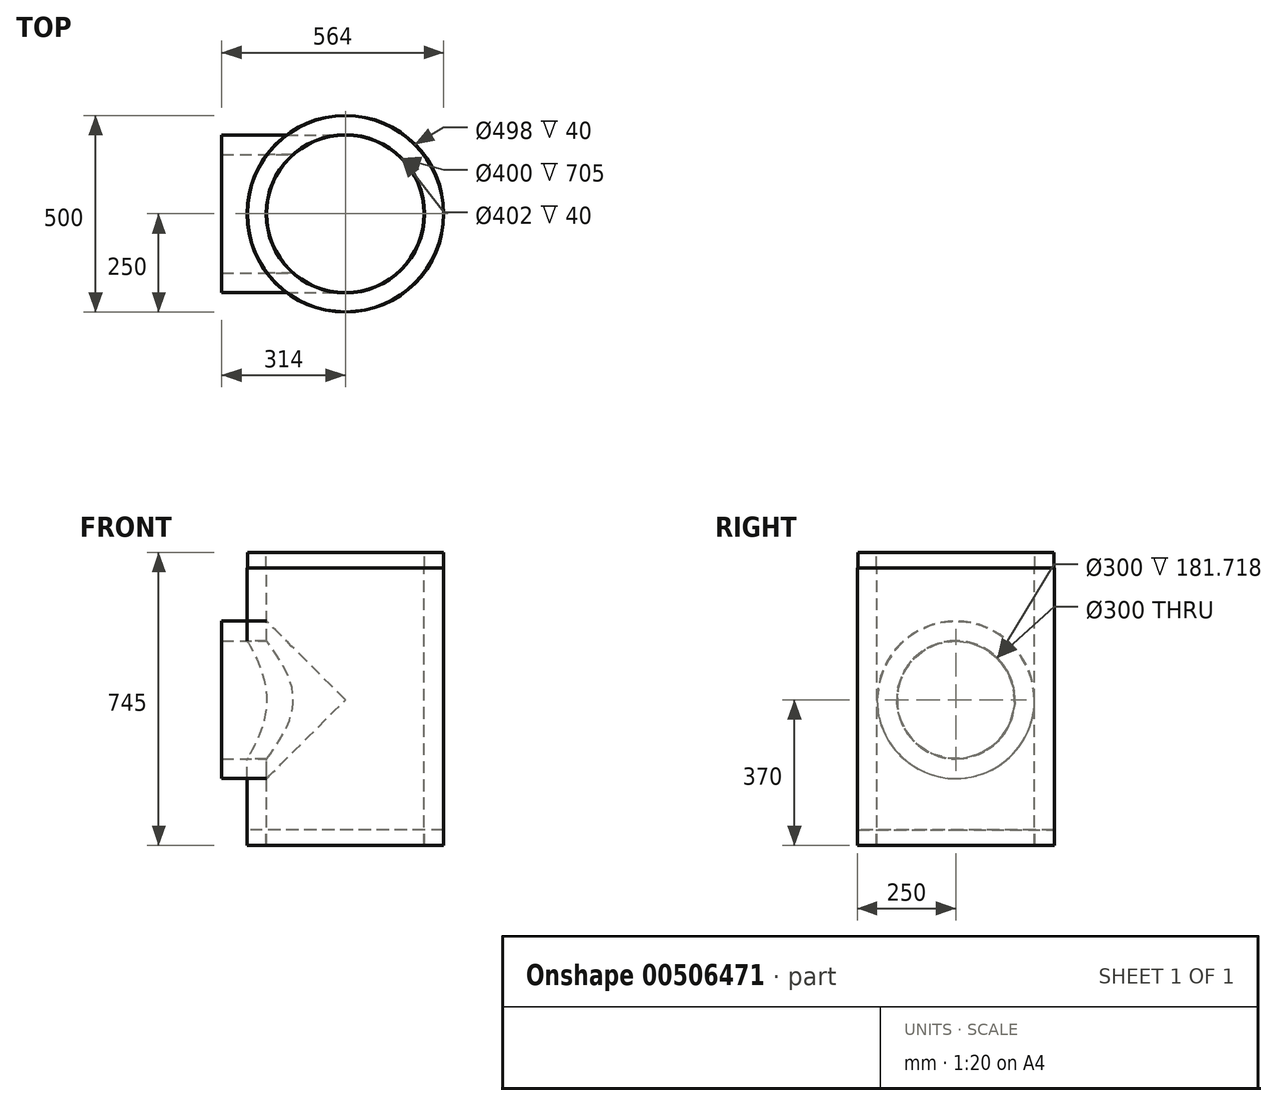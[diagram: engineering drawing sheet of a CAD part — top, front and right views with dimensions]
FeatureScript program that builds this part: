
annotation { "Feature Type Name" : "Feature", "Feature Type Description" : "" }
export const myFeature = defineFeature(function(context is Context, id is Id, definition is map)
    precondition{}
    {
        {
            var Q0;
            Q0=qCreatedBy(makeId("Front.planeOp"),FACE);
            var sketch = newSketch(context, id + "F0", { "sketchPlane" : qUnion([Q0])});
            skLineSegment(sketch, "E0", {"start": v(0, 722.18) * mm, "end": v(0, -793.11) * mm, "construction": true});
            skLineSegment(sketch, "E1", {"start": v(-200, -370) * mm, "end": v(-200, 335) * mm});
            skLineSegment(sketch, "E2", {"start": v(-200, 335) * mm, "end": v(-201, 335) * mm});
            skLineSegment(sketch, "E3", {"start": v(-201, 335) * mm, "end": v(-201, 375) * mm});
            skLineSegment(sketch, "E4", {"start": v(-201, 375) * mm, "end": v(-249, 375) * mm});
            skLineSegment(sketch, "E5", {"start": v(-249, 375) * mm, "end": v(-249, 335) * mm});
            skLineSegment(sketch, "E6", {"start": v(-249, 335) * mm, "end": v(-250, 335) * mm});
            skLineSegment(sketch, "E7", {"start": v(-250, 335) * mm, "end": v(-250, -370) * mm});
            skLineSegment(sketch, "E8", {"start": v(-250, -370) * mm, "end": v(-249, -370) * mm});
            skLineSegment(sketch, "E9", {"start": v(-249, -370) * mm, "end": v(-249, -330) * mm});
            skLineSegment(sketch, "E10", {"start": v(-249, -330) * mm, "end": v(-201, -330) * mm});
            skLineSegment(sketch, "E11", {"start": v(-201, -330) * mm, "end": v(-201, -370) * mm});
            skLineSegment(sketch, "E12", {"start": v(-201, -370) * mm, "end": v(-200, -370) * mm});
            skLineSegment(sketch, "E13", {"start": v(0, 0) * mm, "end": v(-528, 0) * mm, "construction": true});
            skLineSegment(sketch, "E14", {"start": v(0, -150) * mm, "end": v(-314, -150) * mm});
            skLineSegment(sketch, "E15", {"start": v(-314, -150) * mm, "end": v(-314, -200) * mm});
            skLineSegment(sketch, "E16", {"start": v(-314, -200) * mm, "end": v(0, -200) * mm});
            skLineSegment(sketch, "E17", {"start": v(0, -200) * mm, "end": v(0, -150) * mm});
            skLineSegment(sketch, "E18", {"start": v(-314, -150) * mm, "end": v(-314, 0) * mm});
            skLineSegment(sketch, "E19", {"start": v(-314, 0) * mm, "end": v(-264, 0) * mm});
            skLineSegment(sketch, "E20", {"start": v(-264, 0) * mm, "end": v(-264, -150) * mm});
            skSolve(sketch);
        }
        {
            var Q0;
            {var subQ0=sQuery(id+"F0.wireOp",EDGE,"E2");Q0=makeQuery(id+"F0.imprint","IMPRINT",FACE,{"disambiguationData":[TD([[makeQuery(id+"F0.imprint","IMPRINT",EDGE,{"derivedFrom":subQ0}),1.0]])]});}
            var Q1;
            {var subQ0=sQuery(id+"F0.wireOp",EDGE,"E16");var subQ1=sQuery(id+"F0.wireOp",EDGE,"E1");var subQ2=makeQuery(id+"F0.imprint","INTERSECT",VERTEX,{"derivedFrom":[subQ1,subQ0]});Q1=makeQuery(id+"F0.imprint","IMPRINT",FACE,{"disambiguationData":[TD([[makeQuery(id+"F0.imprint","IMPRINT",EDGE,{"disambiguationData":[TD([[subQ2,-1.0]])],"derivedFrom":subQ1}),1.0]])]});}
            var Q2;
            {var subQ0=sQuery(id+"F0.wireOp",EDGE,"E8");Q2=makeQuery(id+"F0.imprint","IMPRINT",FACE,{"disambiguationData":[TD([[makeQuery(id+"F0.imprint","IMPRINT",EDGE,{"derivedFrom":subQ0}),1.0]])]});}
            var Q3;
            Q3=sQuery(id+"F0.wireOp",EDGE,"E0");
            revolve(context, id + "F1", {"entities" : qUnion([Q0, Q1, Q2]), "axis" : qUnion([Q3]), "revolveType" : RevolveType.FULL});
        }
        {
            var Q0;
            {var subQ0=sQuery(id+"F0.wireOp",EDGE,"E18");Q0=makeQuery(id+"F0.imprint","IMPRINT",FACE,{"disambiguationData":[TD([[makeQuery(id+"F0.imprint","IMPRINT",EDGE,{"derivedFrom":subQ0}),-1.0]])]});}
            var Q1;
            {var subQ0=sQuery(id+"F0.wireOp",EDGE,"E15");Q1=makeQuery(id+"F0.imprint","IMPRINT",FACE,{"disambiguationData":[TD([[makeQuery(id+"F0.imprint","IMPRINT",EDGE,{"derivedFrom":subQ0}),1.0]])]});}
            var Q2;
            {var subQ0=sQuery(id+"F0.wireOp",EDGE,"E16");var subQ1=sQuery(id+"F0.wireOp",EDGE,"E1");var subQ2=makeQuery(id+"F0.imprint","INTERSECT",VERTEX,{"derivedFrom":[subQ1,subQ0]});Q2=makeQuery(id+"F0.imprint","IMPRINT",FACE,{"disambiguationData":[TD([[makeQuery(id+"F0.imprint","IMPRINT",EDGE,{"disambiguationData":[TD([[subQ2,-1.0]])],"derivedFrom":subQ1}),1.0]])]});}
            var Q3;
            {var subQ5=sQuery(id+"F0.wireOp",EDGE,"E17");Q3=makeQuery(id+"F0.imprint","IMPRINT",FACE,{"disambiguationData":[TD([[makeQuery(id+"F0.imprint","IMPRINT",EDGE,{"derivedFrom":subQ5}),1.0]])]});}
            var Q4;
            Q4=sQuery(id+"F0.wireOp",EDGE,"E13");
            revolve(context, id + "F2", {"entities" : qUnion([Q0, Q1, Q2, Q3]), "axis" : qUnion([Q4]), "revolveType" : RevolveType.FULL});
        }
        {
            var Q0;
            Q0=makeQuery(id+"F2.opRevolve","SWEPT_FACE",FACE,{"disambiguationData":[OSD([sQuery(id+"F0.wireOp",EDGE,"E15"),sQuery(id+"F0.wireOp",EDGE,"E18")])]});
            var sketch = newSketch(context, id + "F3", { "sketchPlane" : qUnion([Q0])});
            skCircle(sketch, "E21", {"center": v(0, 0) * mm, "radius": 150 * mm});
            skSolve(sketch);
        }
        {
            var Q0;
            Q0=qSketchRegion(id+"F3",true);
            var Q1;
            Q1=makeQuery(id+"F2.opRevolve","SWEPT_FACE",FACE,{"disambiguationData":[OSD([sQuery(id+"F0.wireOp",EDGE,"E17")])]});
            extrude(context, id + "F4", {"entities" : qUnion([Q0]), "operationType" : NewBodyOperationType.REMOVE, "endBound" : BoundingType.UP_TO_SURFACE, "oppositeDirection" : true, "endBoundEntityFace" : qUnion([Q1]), "offsetDistance" : 25 * mm, "depth" : 600 * mm});
        }
        {
            var Q0;
            Q0=makeQuery(id+"F1.opRevolve","SWEPT_FACE",FACE,{"disambiguationData":[OSD([sQuery(id+"F0.wireOp",EDGE,"E4")])]});
            var sketch = newSketch(context, id + "F5", { "sketchPlane" : qUnion([Q0])});
            skCircle(sketch, "E22", {"center": v(0, 0) * mm, "radius": 200 * mm});
            skSolve(sketch);
        }
        {
            var Q0;
            Q0=qSketchRegion(id+"F5",true);
            extrude(context, id + "F6", {"entities" : qUnion([Q0]), "operationType" : NewBodyOperationType.REMOVE, "oppositeDirection" : true, "depth" : 1200 * mm});
        }
    });
